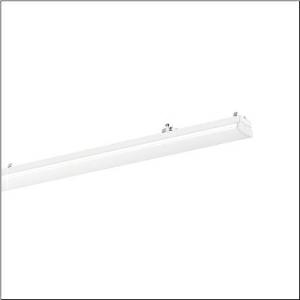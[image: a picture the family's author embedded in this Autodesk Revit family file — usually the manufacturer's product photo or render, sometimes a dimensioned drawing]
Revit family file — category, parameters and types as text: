
# Revit family: licross_11_recessed_opal_mo_51tl1ddn495g
name_source: partatom
category: Lighting Fixtures
units: mm (PartAtom-declared; Revit-internal decimal feet)

## family parameters
Cut with Voids When Loaded = No
Host = Face
Light Source = No
Part Type = Normal
Room Calculation Point = No
Round Connector Dimension = Use Diameter
Shared = No

## types (1)
- --- (1 x LED, 9710 lm, 56.7 W, 4000K)
    Apparent Load = 57 VA
    CIE Flux Codes = 44 73 91 87 100
    Color Rendering = 80
    Color Temperature = 4000K
    Default Elevation = 1800 mm
    Description = Licross 11 recessed opal MO, luminaire insert, of sheet steel, coil coated, white, length: 1.500mm, width: 76mm, height: 87mm, LED rated luminous flux: 9.710lm, light colour: 840, SDCM (Standard Deviation of Colour Matching)MacAdam ≤ 2 SDCM (initial), control gear: DALI 2, with plug, 5-pole, with phase selection, mains connection: 220..240V, AC, 50/60Hz, rated input power: 57W, internal wiring halogen-free, primary optical cover: cover, of PMMA, light emission: direct with ceiling illumination distribution, primary light characteristic: symmetric, protection rating (complete): IP40, insulation class (complete): insulation class I (protective earthing), certification: CE, ENEC, VDE, UKCA, protection symbol: D if used in an environment without relevant dust loads with corresponding accessories, impact resistance: IK06, permissible ambient temperature for indoor applications: -25..+35°C, corresponds to IFS (International Featured Standards) requirements for safety and quality in the food industry, reducing of maximum allowable ambient temperature of 5°C with ceiling mounting, LABS conformity tested according to VDMA 24364:2018-05, The light source and the operating device comply with the requirements of the Ecodesign Regulation (EU) 2019/2020 and are replaceable in accordance with this regulation, packaging unit: 1 piece
    Height = 83 mm
    Lamp = 1 x LED
    Lamp Light Flux = 9710 lm
    Lamp Power = 56.7 W
    Lamp count = 1
    Length = 1500 mm
    Luminous efficacy = 171 lm/W
    Manufacturer = Siteco
    ModVariant = No
    Model = 51TL1DDN495G
    Mounting Place = Ceiling
    Mounting Type = Pendant
    Number of Poles = 1
    OnlyDefault = Yes
    Power Factor = 1
    Product Name = Licross 11 recessed opal MO
    Product group = luminaire insert | ceiling pendant
    ProductGroupID = 901
    Protection Class = Protection class I
    Protection Degree = IP 40
    RLX_Detail_Level = 1
    RLX_Emergency_Light_Flux = 0 lm
    RLX_Emergency_Type = 0
    RLX_Emergency_Type_DB = No
    RlxData = <blob elided: 27005 chars, md5=50ce220d>
    Socket = socket
    Standby Power = 0 W
    System Light Flux = 9710 lm
    System Power = 57 W
    Type Comments = factory setting: luminous flux: 100 % | dim-lin: 254 | 378 mA
    Type Image = l_1313666.jpg
    URL = http://relux.com
    VarID = @adj_083889
    Voltage = 0 V
    Weight = 0.00 kg
    Width = 76 mm

## geometry (parser evidence)
native form markers: Blend x4, Sweep x14
no freeform markers — native parametric forms only
